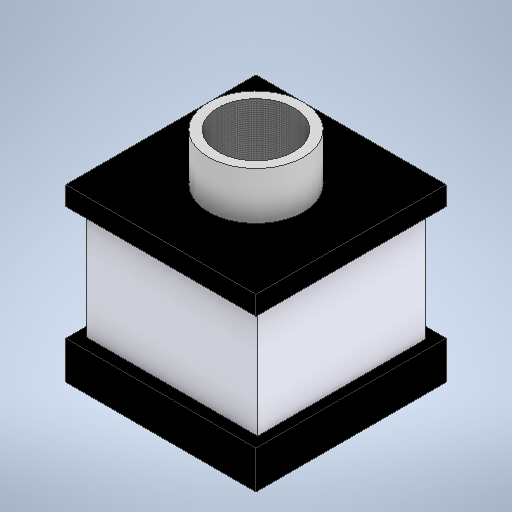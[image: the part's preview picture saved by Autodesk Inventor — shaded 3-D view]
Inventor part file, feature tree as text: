
AUTODESK INVENTOR PART (.ipt)
format: ipt  version: 2025.2 (Build 292293000, 293)  size: 271,360 bytes
history: native  units: mm
features: extrude x5, sketch x5, projected_geometry x2
ambient origin geometry x8: Origin, YZ Plane, XZ Plane, XY Plane, X Axis, Y Axis, Z Axis, Center Point
bodies: Solid1 (feature_tree)
feature tree (12):
  extrude  "Extrusion1"  Depth=200.0mm
  extrude  "Extrusion2"  Depth=180.0mm
  extrude  "Extrusion3"  Depth=20.0mm TaperAngle=0.0deg
  extrude  "Extrusion4"  Depth=50.0mm TaperAngle=0.0deg
  extrude  "Extrusion5"  Depth=80.0mm TaperAngle=0.0deg
  sketch  "Sketch1"  dims[d0=200.0mm d1=200.0mm]
  sketch  "Sketch2"  dims[d2=40.0mm d3=0.0mm d4=180.0mm]
  projected_geometry  "Projected Loop1"
  sketch  "Sketch3"  dims[d5=120.0mm d6=0.0mm d7=20.0mm d8=0.0mm]
  projected_geometry  "Projected Loop2"
  sketch  "Sketch4"  dims[d9=100.0mm d10=50.0mm d11=0.0mm]
  sketch  "Sketch5"  dims[d12=80.0mm d13=80.0mm d14=0.0mm]
